AUTODESK INVENTOR PART (.ipt)
format: ipt  version: 2021.3 (Build 253353010, 353A)  size: 84,480 bytes
history: native  units: mm
features: reference x3, other x3, sketch x1
ambient origin geometry x8: Origin, YZ Plane, XZ Plane, XY Plane, X Axis, Y Axis, Z Axis, Center Point
feature tree (7):
  sketch  "Skizze1"
  reference  "Referenz1"
  reference  "Referenz2"
  reference  "Referenz3"
  other  "Baugruppe18"
  other  "BackPlate:1"
  other  "Intel_RealSense_D455_CAD_external_v2:1"
